# Revit family: CONV_Pholc_GnrlPrpseLmnrs_BellmanWall
name_source: partatom
category: Lighting Fixtures
revit_build: Autodesk Revit 2015 (Build: 20140606_1530(x64)
units: mm (PartAtom-declared; Revit-internal decimal feet)

## types (2) — shared parameters
AssetType = Fixed
BIMObjectName = CONV_Pholc_GnrlPrpseLmnrs_BellmanWall
Brand = Pholc
BulbIncluded = No
CableType = PVC
Category = Wall
Collection = Soft Reflections
Color Filter = 16777215
ConvergoRefNr = 0103-1703-0002-SE
Description = A simple and soft form of shade put together with a masculine and stable arm
Designer = Sabina Grubbeson
Dimming Lamp Color Temperature Shift = <None>
DurationUnit = Year
ExpiringDate = 07/2017
IfcExportAs = IfcLightFixtureType
IfcExportType = NOTDEFINED
Light Source Symbol Length = 609 mm  [stored 1.99803 ft]
LightFixtureMountingType = Cable
LightFixturePlacingType = Wall
ManufacterURL = http://www.pholc.se
Manufacturer = Pholc
ManufacturerName = Pholc
Material = Steel
Model = Bellman Wall
NBSDescription = General purpose luminaires
NBSReference = 90-60-50/405
Name = GnrlPrpseLmnrs_BellmanWall
NominalLength = 2076 mm
NominalWidth = 160 mm  [stored 0.524934 ft]
NumberOfSources = 1
ProductInformation = A simple and soft form of shade put together with a masculine and stable arm
Shape = Sculptured
Socket = E27 Base
Spot Beam Angle = 30.00°
Spot Field Angle = 90.00°
Tilt Angle = 90.00°
TotalWattage = 42 W
URL = http://www.pholc.se
Uniclass2 = 90-65-49/434
Uniclass2015Description = Luminaires, lighting track and lighting accessories
Uniclass2015Reference = Pr_70_70_48
Version = 1
VersionDate = 15/03/2017
WarrantyDurationUnit = Year
zero-valued in all types: MaintenanceFactor

## per-type parameters (varying)
| type | ArticleNumber | Default Elevation | LightFixtureMainMaterial | LightFixtureSecondaryMaterial | ModelReference | NominalHeight | Size |
| Black | 311215 | 1800 mm  [stored 5.90551 ft] | Steel Black | PVC Black | 311215 | 460 mm  [stored 1.50919 ft] | 160x2076x460mm |
| White | 311213 | 0 mm  [stored 0 ft] | Steel White | PVC White | 311213 | 0 mm  [stored 0 ft] | 160x2076x360mm |

note: column(s) folded — value = type name in every type: Color

note: [stored X ft] marks values corroborated as IEEE doubles in the binary element streams (Revit-internal decimal feet)

## geometry (parser evidence)
native form markers: Sweep x2
no freeform markers — native parametric forms only
